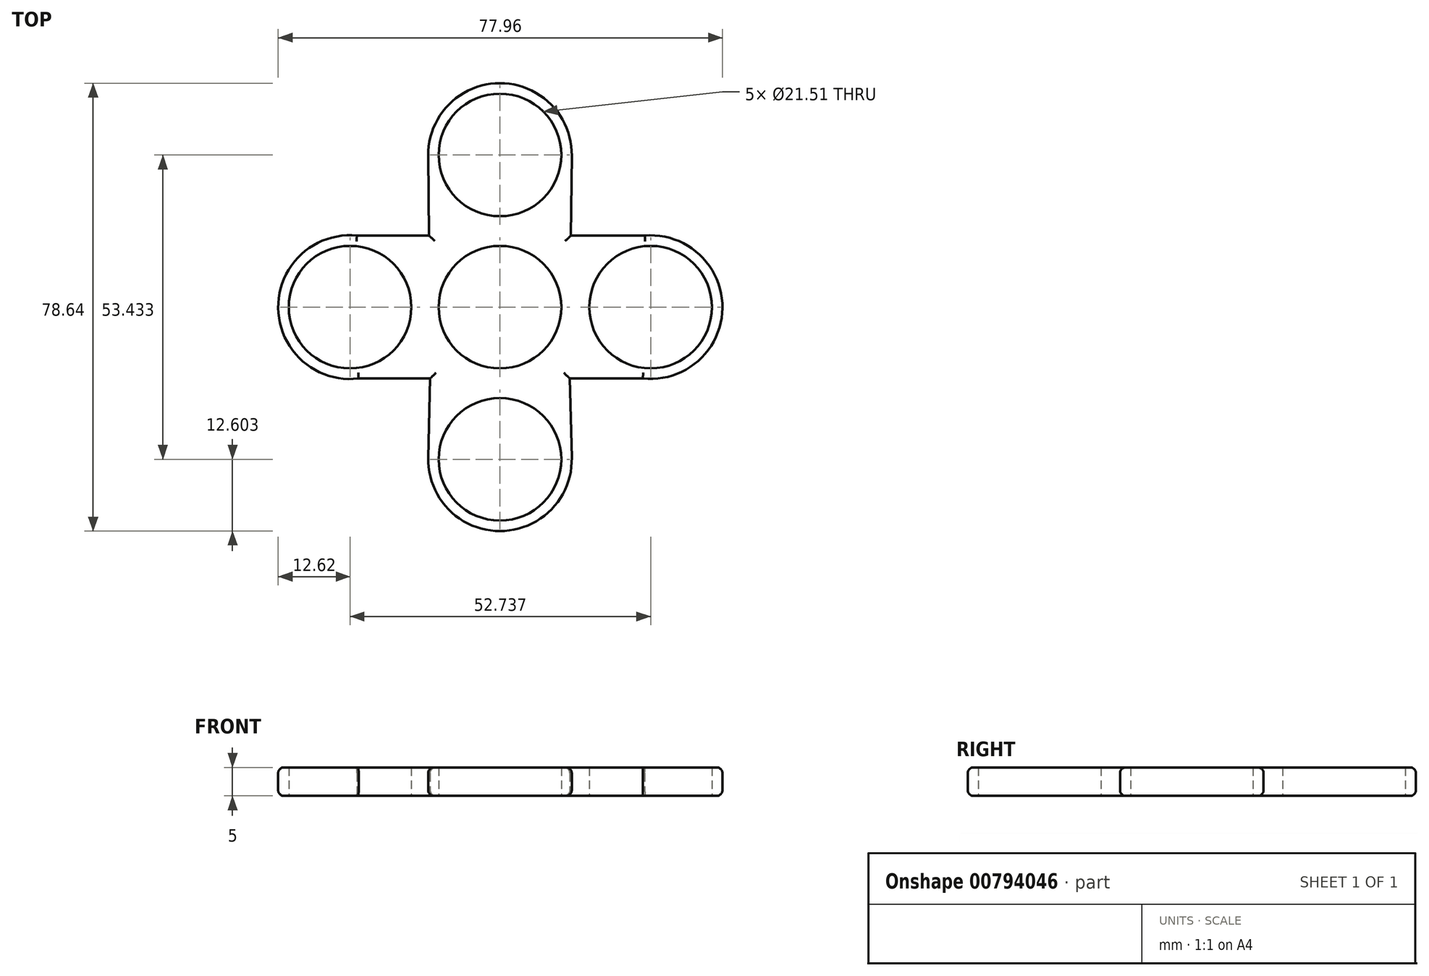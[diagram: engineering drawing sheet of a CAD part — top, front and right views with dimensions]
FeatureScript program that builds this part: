
annotation { "Feature Type Name" : "Feature", "Feature Type Description" : "" }
export const myFeature = defineFeature(function(context is Context, id is Id, definition is map)
    precondition{}
    {
        {
            var Q0;
            Q0=qCreatedBy(makeId("Top.planeOp"),FACE);
            var sketch = newSketch(context, id + "F0", { "sketchPlane" : qUnion([Q0])});
            skCircle(sketch, "E0", {"center": v(-26.3, 0) * mm, "radius": 12.62 * mm});
            skCircle(sketch, "E1", {"center": v(0, 26.72) * mm, "radius": 12.6 * mm});
            skCircle(sketch, "E2", {"center": v(26.44, 0) * mm, "radius": 12.6 * mm});
            skCircle(sketch, "E3", {"center": v(0, -26.72) * mm, "radius": 12.6 * mm});
            skLineSegment(sketch, "E4", {"start": v(-27.53, 12.56) * mm, "end": v(-12.45, 12.58) * mm});
            skLineSegment(sketch, "E5", {"start": v(-12.45, 12.58) * mm, "end": v(-12.6, 26.58) * mm});
            skLineSegment(sketch, "E6", {"start": v(-27.8, -12.53) * mm, "end": v(-12.25, -12.53) * mm});
            skLineSegment(sketch, "E7", {"start": v(-12.25, -12.53) * mm, "end": v(-12.6, -26.4) * mm});
            skLineSegment(sketch, "E8.MirrorCS", {"start": v(12.45, 12.58) * mm, "end": v(12.6, 26.58) * mm});
            skLineSegment(sketch, "E9.MirrorCS", {"start": v(27.53, 12.56) * mm, "end": v(12.45, 12.58) * mm});
            skLineSegment(sketch, "E10.MirrorCS", {"start": v(27.8, -12.53) * mm, "end": v(12.25, -12.53) * mm});
            skLineSegment(sketch, "E11.MirrorCS", {"start": v(12.25, -12.53) * mm, "end": v(12.6, -26.4) * mm});
            skCircle(sketch, "E12", {"center": v(0, 0) * mm, "radius": 10.75 * mm});
            skCircle(sketch, "E13", {"center": v(-26.3, 0) * mm, "radius": 10.75 * mm});
            skCircle(sketch, "E14", {"center": v(0, -26.72) * mm, "radius": 10.75 * mm});
            skCircle(sketch, "E15", {"center": v(0, 26.72) * mm, "radius": 10.75 * mm});
            skCircle(sketch, "E16", {"center": v(26.44, 0) * mm, "radius": 10.75 * mm});
            skSolve(sketch);
        }
        {
            var Q0;
            Q0 = qSketchRegion(id + "F0", true);
            extrude(context, id + "F1", {"entities" : qUnion([Q0]), "depth" : 5 * mm, "offsetDistance" : 25 * mm});
        }
        {
            var Q0;
            Q0=makeQuery(id+"F1.opExtrude","CAP_EDGE",EDGE,{"disambiguationData":[OSD([sQuery(id+"F0.wireOp",EDGE,"E4")])],"isStart":false});
            var Q1;
            Q1=makeQuery(id+"F1.opExtrude","CAP_EDGE",EDGE,{"disambiguationData":[OSD([sQuery(id+"F0.wireOp",EDGE,"E0")])],"isStart":false});
            var Q2;
            Q2=makeQuery(id+"F1.opExtrude","CAP_EDGE",EDGE,{"disambiguationData":[OSD([sQuery(id+"F0.wireOp",EDGE,"E5")])],"isStart":false});
            var Q3;
            Q3=makeQuery(id+"F1.opExtrude","CAP_EDGE",EDGE,{"disambiguationData":[OSD([sQuery(id+"F0.wireOp",EDGE,"E1")])],"isStart":false});
            var Q4;
            Q4=makeQuery(id+"F1.opExtrude","CAP_EDGE",EDGE,{"disambiguationData":[OSD([sQuery(id+"F0.wireOp",EDGE,"E6")])],"isStart":false});
            var Q5;
            Q5=makeQuery(id+"F1.opExtrude","CAP_EDGE",EDGE,{"disambiguationData":[OSD([sQuery(id+"F0.wireOp",EDGE,"E7")])],"isStart":false});
            var Q6;
            Q6=makeQuery(id+"F1.opExtrude","CAP_EDGE",EDGE,{"disambiguationData":[OSD([sQuery(id+"F0.wireOp",EDGE,"E3")])],"isStart":false});
            var Q7;
            Q7=makeQuery(id+"F1.opExtrude","CAP_EDGE",EDGE,{"disambiguationData":[OSD([sQuery(id+"F0.wireOp",EDGE,"E11.MirrorCS")])],"isStart":false});
            var Q8;
            Q8=makeQuery(id+"F1.opExtrude","CAP_EDGE",EDGE,{"disambiguationData":[OSD([sQuery(id+"F0.wireOp",EDGE,"E10.MirrorCS")])],"isStart":false});
            var Q9;
            Q9=makeQuery(id+"F1.opExtrude","CAP_EDGE",EDGE,{"disambiguationData":[OSD([sQuery(id+"F0.wireOp",EDGE,"E2")])],"isStart":false});
            var Q10;
            Q10=makeQuery(id+"F1.opExtrude","CAP_EDGE",EDGE,{"disambiguationData":[OSD([sQuery(id+"F0.wireOp",EDGE,"E9.MirrorCS")])],"isStart":false});
            fillet(context, id + "F2", {"entities" : qUnion([Q0, Q1, Q2, Q3, Q4, Q5, Q6, Q7, Q8, Q9, Q10]), "radius" : 1 * mm, "tangentPropagation" : true, "allowEdgeOverflow" : false});
        }
        {
            var Q0;
            Q0=makeQuery(id+"F1.opExtrude","CAP_EDGE",EDGE,{"disambiguationData":[OSD([sQuery(id+"F0.wireOp",EDGE,"E6")])],"isStart":true});
            var Q1;
            Q1=makeQuery(id+"F1.opExtrude","CAP_EDGE",EDGE,{"disambiguationData":[OSD([sQuery(id+"F0.wireOp",EDGE,"E0")])],"isStart":true});
            var Q2;
            Q2=makeQuery(id+"F1.opExtrude","CAP_EDGE",EDGE,{"disambiguationData":[OSD([sQuery(id+"F0.wireOp",EDGE,"E4")])],"isStart":true});
            var Q3;
            Q3=makeQuery(id+"F1.opExtrude","CAP_EDGE",EDGE,{"disambiguationData":[OSD([sQuery(id+"F0.wireOp",EDGE,"E5")])],"isStart":true});
            var Q4;
            Q4=makeQuery(id+"F1.opExtrude","CAP_EDGE",EDGE,{"disambiguationData":[OSD([sQuery(id+"F0.wireOp",EDGE,"E1")])],"isStart":true});
            var Q5;
            Q5=makeQuery(id+"F1.opExtrude","CAP_EDGE",EDGE,{"disambiguationData":[OSD([sQuery(id+"F0.wireOp",EDGE,"E8.MirrorCS")])],"isStart":true});
            var Q6;
            Q6=makeQuery(id+"F1.opExtrude","CAP_EDGE",EDGE,{"disambiguationData":[OSD([sQuery(id+"F0.wireOp",EDGE,"E9.MirrorCS")])],"isStart":true});
            var Q7;
            Q7=makeQuery(id+"F1.opExtrude","CAP_EDGE",EDGE,{"disambiguationData":[OSD([sQuery(id+"F0.wireOp",EDGE,"E2")])],"isStart":true});
            var Q8;
            Q8=makeQuery(id+"F1.opExtrude","CAP_EDGE",EDGE,{"disambiguationData":[OSD([sQuery(id+"F0.wireOp",EDGE,"E10.MirrorCS")])],"isStart":true});
            var Q9;
            Q9=makeQuery(id+"F1.opExtrude","CAP_EDGE",EDGE,{"disambiguationData":[OSD([sQuery(id+"F0.wireOp",EDGE,"E11.MirrorCS")])],"isStart":true});
            var Q10;
            Q10=makeQuery(id+"F1.opExtrude","CAP_EDGE",EDGE,{"disambiguationData":[OSD([sQuery(id+"F0.wireOp",EDGE,"E7")])],"isStart":true});
            var Q11;
            Q11=makeQuery(id+"F1.opExtrude","CAP_EDGE",EDGE,{"disambiguationData":[OSD([sQuery(id+"F0.wireOp",EDGE,"E3")])],"isStart":true});
            fillet(context, id + "F3", {"entities" : qUnion([Q0, Q1, Q2, Q3, Q4, Q5, Q6, Q7, Q8, Q9, Q10, Q11]), "radius" : 1 * mm, "tangentPropagation" : true, "allowEdgeOverflow" : false});
        }
    });
